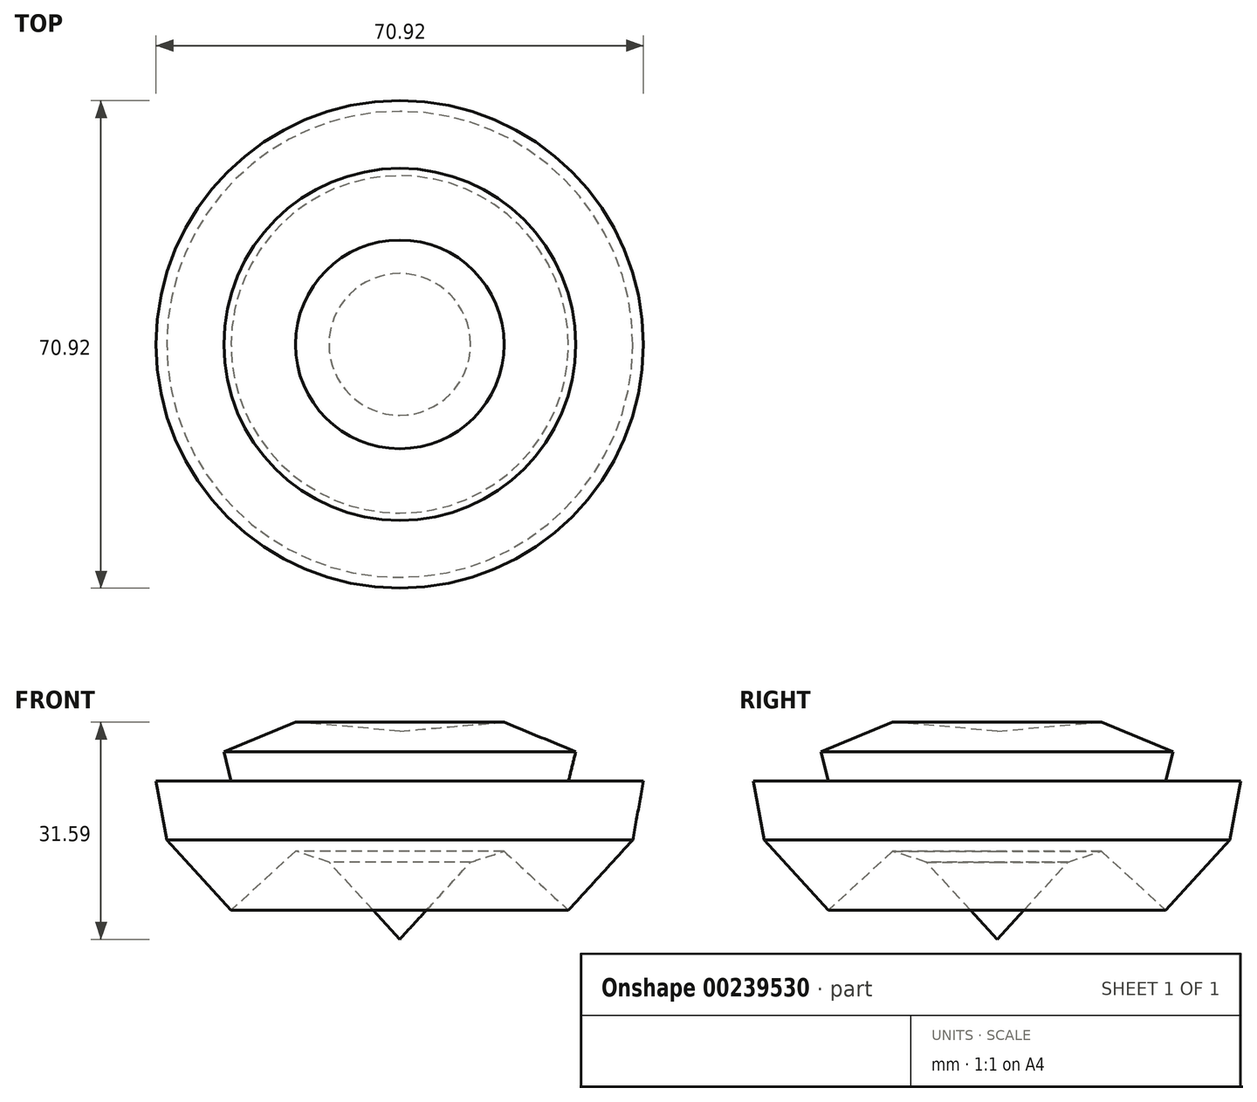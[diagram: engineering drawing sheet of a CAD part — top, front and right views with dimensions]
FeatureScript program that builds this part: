
annotation { "Feature Type Name" : "Feature", "Feature Type Description" : "" }
export const myFeature = defineFeature(function(context is Context, id is Id, definition is map)
    precondition{}
    {
        {
            var Q0;
            Q0=qCreatedBy(makeId("Front.planeOp"),FACE);
            var sketch = newSketch(context, id + "F0", { "sketchPlane" : qUnion([Q0])});
            skLineSegment(sketch, "E0", {"start": v(0, 0) * mm, "end": v(10.3, 11.23) * mm});
            skLineSegment(sketch, "E1", {"start": v(10.3, 11.23) * mm, "end": v(0, 11.23) * mm});
            skLineSegment(sketch, "E2", {"start": v(0, 11.23) * mm, "end": v(0, 0) * mm});
            skLineSegment(sketch, "E3", {"start": v(10.3, 11.23) * mm, "end": v(15.18, 12.8) * mm});
            skLineSegment(sketch, "E4", {"start": v(15.18, 12.8) * mm, "end": v(24.54, 4.22) * mm});
            skLineSegment(sketch, "E5", {"start": v(24.54, 4.22) * mm, "end": v(33.9, 14.42) * mm});
            skLineSegment(sketch, "E6", {"start": v(33.9, 14.42) * mm, "end": v(24.54, 23) * mm});
            skLineSegment(sketch, "E7", {"start": v(24.54, 23) * mm, "end": v(15.18, 12.8) * mm});
            skLineSegment(sketch, "E8", {"start": v(15.18, 12.8) * mm, "end": v(33.9, 14.42) * mm});
            skLineSegment(sketch, "E9", {"start": v(24.54, 23) * mm, "end": v(15.18, 31.6) * mm});
            skLineSegment(sketch, "E10", {"start": v(15.18, 31.6) * mm, "end": v(0, 30.28) * mm});
            skLineSegment(sketch, "E11", {"start": v(0, 30.28) * mm, "end": v(10.3, 11.23) * mm});
            skLineSegment(sketch, "E12", {"start": v(15.18, 31.6) * mm, "end": v(0, 11.23) * mm});
            skLineSegment(sketch, "E13", {"start": v(0, 30.28) * mm, "end": v(0, 11.23) * mm});
            skLineSegment(sketch, "E14", {"start": v(15.18, 31.6) * mm, "end": v(25.6, 27.28) * mm});
            skLineSegment(sketch, "E15", {"start": v(25.6, 27.28) * mm, "end": v(24.54, 23) * mm});
            skLineSegment(sketch, "E16", {"start": v(24.54, 23) * mm, "end": v(35.46, 23) * mm});
            skLineSegment(sketch, "E17", {"start": v(35.46, 23) * mm, "end": v(33.9, 14.42) * mm});
            skSolve(sketch);
        }
        {
            var Q0;
            Q0 = qSketchRegion(id + "F0", true);
            var Q1;
            Q1=sQuery(id+"F0.wireOp",EDGE,"E13");
            revolve(context, id + "F1", {"entities" : qUnion([Q0]), "axis" : qUnion([Q1]), "revolveType" : RevolveType.FULL});
        }
    });
